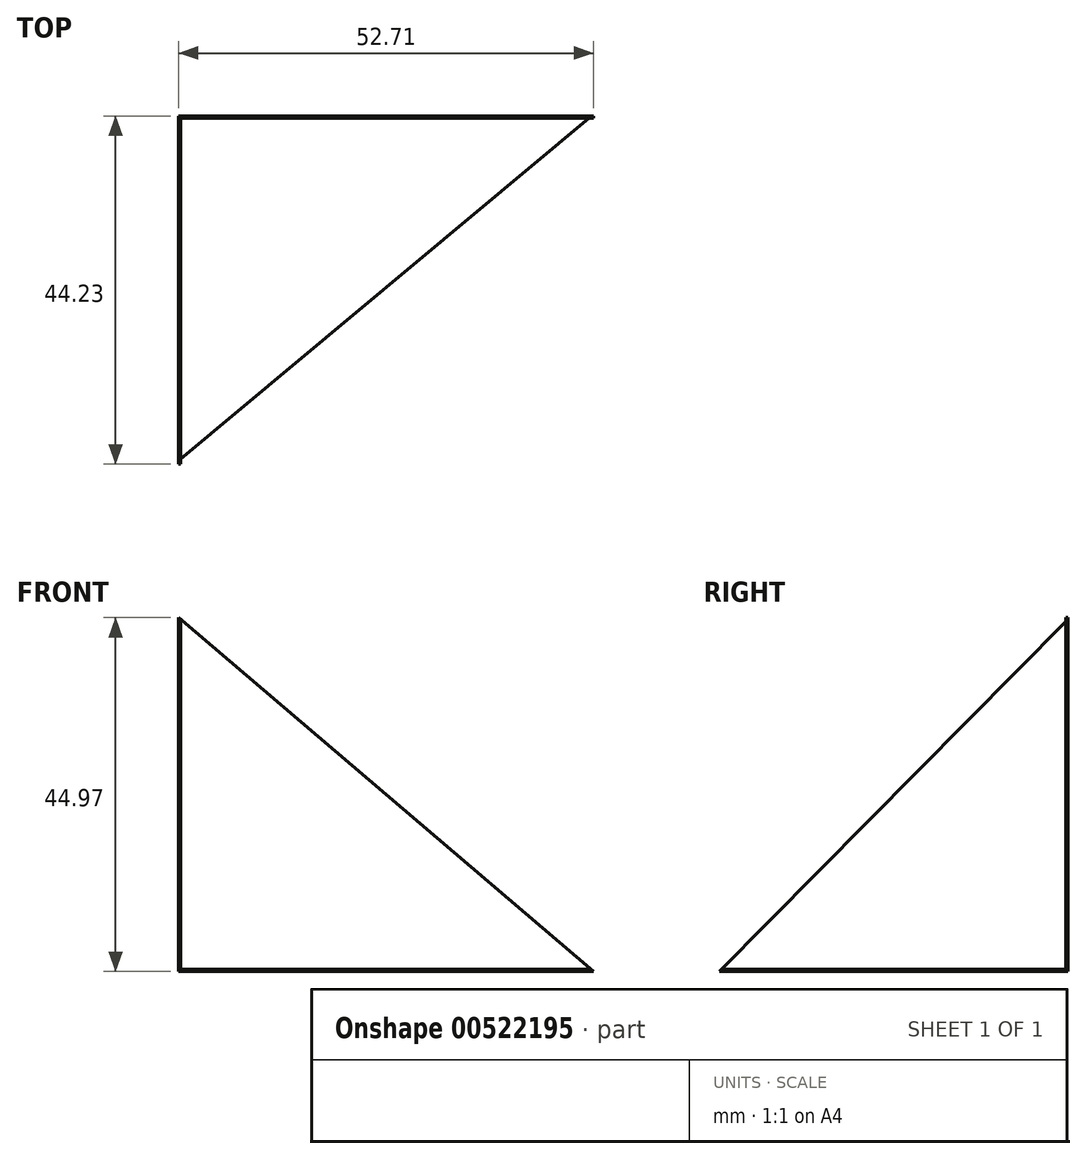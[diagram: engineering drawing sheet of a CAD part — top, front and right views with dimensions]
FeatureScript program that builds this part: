
annotation { "Feature Type Name" : "Feature", "Feature Type Description" : "" }
export const myFeature = defineFeature(function(context is Context, id is Id, definition is map)
    precondition{}
    {
        {
            var Q0;
            Q0=qCreatedBy(makeId("Front.planeOp"),FACE);
            var sketch = newSketch(context, id + "F0", { "sketchPlane" : qUnion([Q0])});
            skLineSegment(sketch, "E0", {"start": v(0, 0) * mm, "end": v(0, 44.97) * mm});
            skLineSegment(sketch, "E1", {"start": v(0, 44.97) * mm, "end": v(52.7, 0) * mm});
            skLineSegment(sketch, "E2", {"start": v(52.7, 0) * mm, "end": v(0, 0) * mm});
            skSolve(sketch);
        }
        {
            var Q0;
            Q0=makeQuery(id+"F0.imprint","IMPRINT",FACE,{"disambiguationData":[TD([[makeQuery(id+"F0.imprint","IMPRINT",EDGE,{"derivedFrom":sQuery(id+"F0.wireOp",EDGE,"E0")}),-1.0]])]});
            extrude(context, id + "F1", {"entities" : qUnion([Q0]), "depth" : 0.25 * mm, "offsetDistance" : 25.4 * mm});
        }
        {
            var Q0;
            Q0=qCreatedBy(makeId("Right.planeOp"),FACE);
            var sketch = newSketch(context, id + "F2", { "sketchPlane" : qUnion([Q0])});
            skLineSegment(sketch, "E3", {"start": v(0, 0) * mm, "end": v(-44.23, 0) * mm});
            skLineSegment(sketch, "E4", {"start": v(-44.23, 0) * mm, "end": v(0, 44.74) * mm});
            skLineSegment(sketch, "E5", {"start": v(0, 44.74) * mm, "end": v(0, 0) * mm});
            skSolve(sketch);
        }
        {
            var Q0;
            Q0=makeQuery(id+"F2.imprint","IMPRINT",FACE,{"disambiguationData":[TD([[makeQuery(id+"F2.imprint","IMPRINT",EDGE,{"derivedFrom":sQuery(id+"F2.wireOp",EDGE,"E3")}),-1.0]])]});
            extrude(context, id + "F3", {"entities" : qUnion([Q0]), "operationType" : NewBodyOperationType.ADD, "depth" : 0.25 * mm, "offsetDistance" : 25.4 * mm});
        }
        {
            var Q0;
            Q0=qCreatedBy(makeId("Top.planeOp"),FACE);
            var sketch = newSketch(context, id + "F4", { "sketchPlane" : qUnion([Q0])});
            skLineSegment(sketch, "E6", {"start": v(0, -43.8) * mm, "end": v(52.42, 0) * mm});
            skLineSegment(sketch, "E7", {"start": v(52.42, 0) * mm, "end": v(0, 0) * mm});
            skLineSegment(sketch, "E8", {"start": v(0, 0) * mm, "end": v(0, -43.8) * mm});
            skSolve(sketch);
        }
        {
            var Q0;
            Q0=makeQuery(id+"F4.imprint","IMPRINT",FACE,{"disambiguationData":[TD([[makeQuery(id+"F4.imprint","IMPRINT",EDGE,{"derivedFrom":sQuery(id+"F4.wireOp",EDGE,"E6")}),1.0]])]});
            extrude(context, id + "F5", {"entities" : qUnion([Q0]), "operationType" : NewBodyOperationType.ADD, "depth" : 0.25 * mm, "offsetDistance" : 25.4 * mm});
        }
    });
